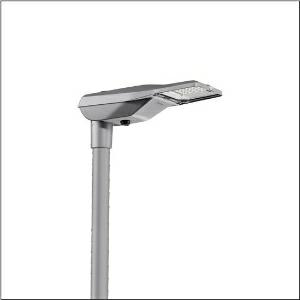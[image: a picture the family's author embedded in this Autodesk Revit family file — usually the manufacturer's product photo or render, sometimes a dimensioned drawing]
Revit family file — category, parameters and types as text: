
# Revit family: streetlight_sl_21_iq_micro___p0_8a_5xe1u31u08cb_c8d0
name_source: partatom
category: Lighting Fixtures
units: mm (PartAtom-declared; Revit-internal decimal feet)

## family parameters
Cut with Voids When Loaded = No
Host = Face
Light Source = No
Part Type = Normal
Room Calculation Point = No
Round Connector Dimension = Use Diameter
Shared = No

## types (1)
- --- (1 x LED, 2890 lm, 19.1 W, 3000K)
    Apparent Load = 19 VA
    CIE Flux Codes = 33 69 96 100 100
    Color Rendering = 70
    Color Temperature = 3000K
    Default Elevation = 1800 mm
    Description = Streetlight SL 21 iQ micro, mast luminaire, primary light control with lens, of PMMA, primary optical cover: cover, of toughened safety glass, transparent, light distribution: P0.8a, light emission: direct distribution, primary light characteristic: asymmetric, installation type: post-top, side-entry, LED, High Power LED, rated luminous flux: 2.890lm, luminous efficacy: 151lm/W, light colour: 730, colour temperature: 3000K, control gear: iQ-Street Remote, D4i with power reduction, control: pre-setting: logarithmic dimming characteristic, Street-Remote, Auto-Match, Temp-Guard, Lumen-Switch, Night-Set, Smart-Wire, Light-Fading, Desk-Remote (wireless, voltage-free reading and setting of iQ features in the workshop via application-optimized NFC function/RFID function), optimised constant luminous flux control (CLO 2.0), mains connection: 220..240V, AC, 50/60Hz, start of lifetime: 19W, end of service life: 20W, reduction: 9W, luminaire housing, of diecast aluminium, powder-coated, SITECO metallic grey (DB 702S), corrosivity category C5 high according to DIN EN ISO 12944, please order mast flange separately, inclination adjustable: 0°, 5°, 10°, 15°, sealing non-destructively replaceable, multi-level sealing system, length: 528mm, width: 235mm, height: 110mm, mast flange for spigot size: 42mm (side-entry): 5XC10008XM4, 60/48mm (side-entry/post-top): 5XC10108XM2, 76/60mm (side-entry/post-top): 5XC10108XM1, mounting height: 4..8m, Smart Interface below, protection rating (complete): IP66, insulation class (complete): insulation class II (safety insulation), certification: CE, ENEC, ENEC+, VDE, impact resistance: IK10, permissible operating ambient temperature for outdoor applications: -40..+50°C, standard-compliant lighting for roads and squares, packaging unit: 1 piece

Light Distribution: P0.8a
    Height = 110 mm
    Lamp = 1 x LED
    Lamp Light Flux = 2890 lm
    Lamp Power = 19.1 W
    Lamp count = 1
    Length = 528 mm
    Luminous efficacy = 151 lm/W
    Manufacturer = Siteco
    ModVariant = No
    Model = 5XE1U31U08CB
    Number of Poles = 1
    OnlyDefault = Yes
    Power Factor = 1
    Product Name = Streetlight SL 21 iQ micro | P0.8a
    Product group = mast luminaire | pylon top
    ProductGroupID = 6100
    Protection Class = Protection class II
    Protection Degree = IP 66
    RLX_Detail_Level = 1
    RLX_Emergency_Light_Flux = 0 lm
    RLX_Emergency_Type = 0
    RLX_Emergency_Type_DB = No
    RlxData = <blob elided: 99085 chars, md5=07306974>
    Socket = socket
    Standby Power = 0 W
    System Light Flux = 2890 lm
    System Power = 19 W
    Type Comments = factory setting: luminous flux: 100 % | dim-lin: 254 | 387 mA
    Type Image = l_1277290.jpg
    URL = http://relux.com
    VarID = @adj_080707
    Voltage = 0 V
    Weight = 0.00 kg
    Width = 235 mm

## geometry (parser evidence)
native form markers: Blend x4, Sweep x9
no freeform markers — native parametric forms only
